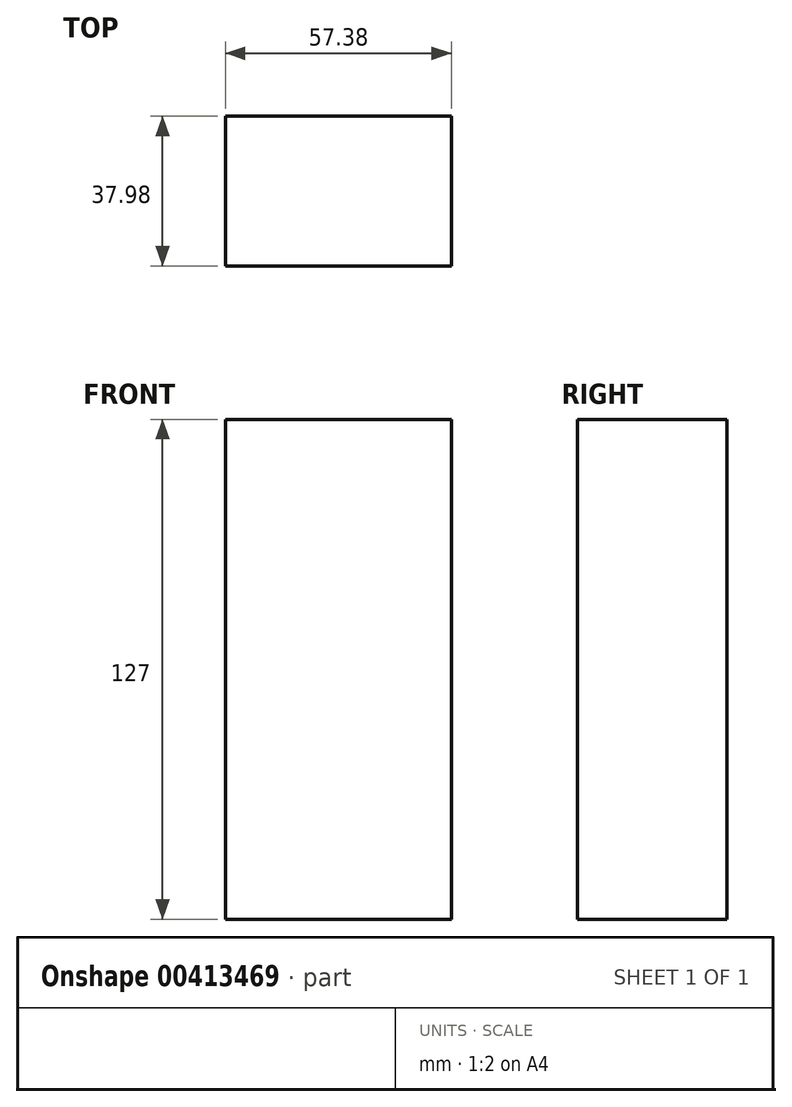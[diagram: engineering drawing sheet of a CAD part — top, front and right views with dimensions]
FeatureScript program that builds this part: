
annotation { "Feature Type Name" : "Feature", "Feature Type Description" : "" }
export const myFeature = defineFeature(function(context is Context, id is Id, definition is map)
    precondition{}
    {
        {
            var Q0;
            Q0=qCreatedBy(makeId("Top.planeOp"),FACE);
            var sketch = newSketch(context, id + "F0", { "sketchPlane" : qUnion([Q0])});
            skLineSegment(sketch, "E0.bottom", {"start": v(28.7, 19) * mm, "end": v(-28.7, 19) * mm});
            skLineSegment(sketch, "E0.top", {"start": v(28.7, -19) * mm, "end": v(-28.7, -19) * mm});
            skLineSegment(sketch, "E0.left", {"start": v(28.7, 19) * mm, "end": v(28.7, -19) * mm});
            skLineSegment(sketch, "E0.right", {"start": v(-28.7, 19) * mm, "end": v(-28.7, -19) * mm});
            skPoint(sketch, "E0.middle", {"position": v(0, 0) * mm});
            skSolve(sketch);
        }
        {
            var Q0;
            Q0=makeQuery(id+"F0.imprint","IMPRINT",FACE,{"disambiguationData":[TD([[makeQuery(id+"F0.imprint","IMPRINT",EDGE,{"derivedFrom":sQuery(id+"F0.wireOp",EDGE,"E0.bottom")}),1.0]])]});
            extrude(context, id + "F1", {"entities" : qUnion([Q0]), "depth" : 127 * mm});
        }
    });
